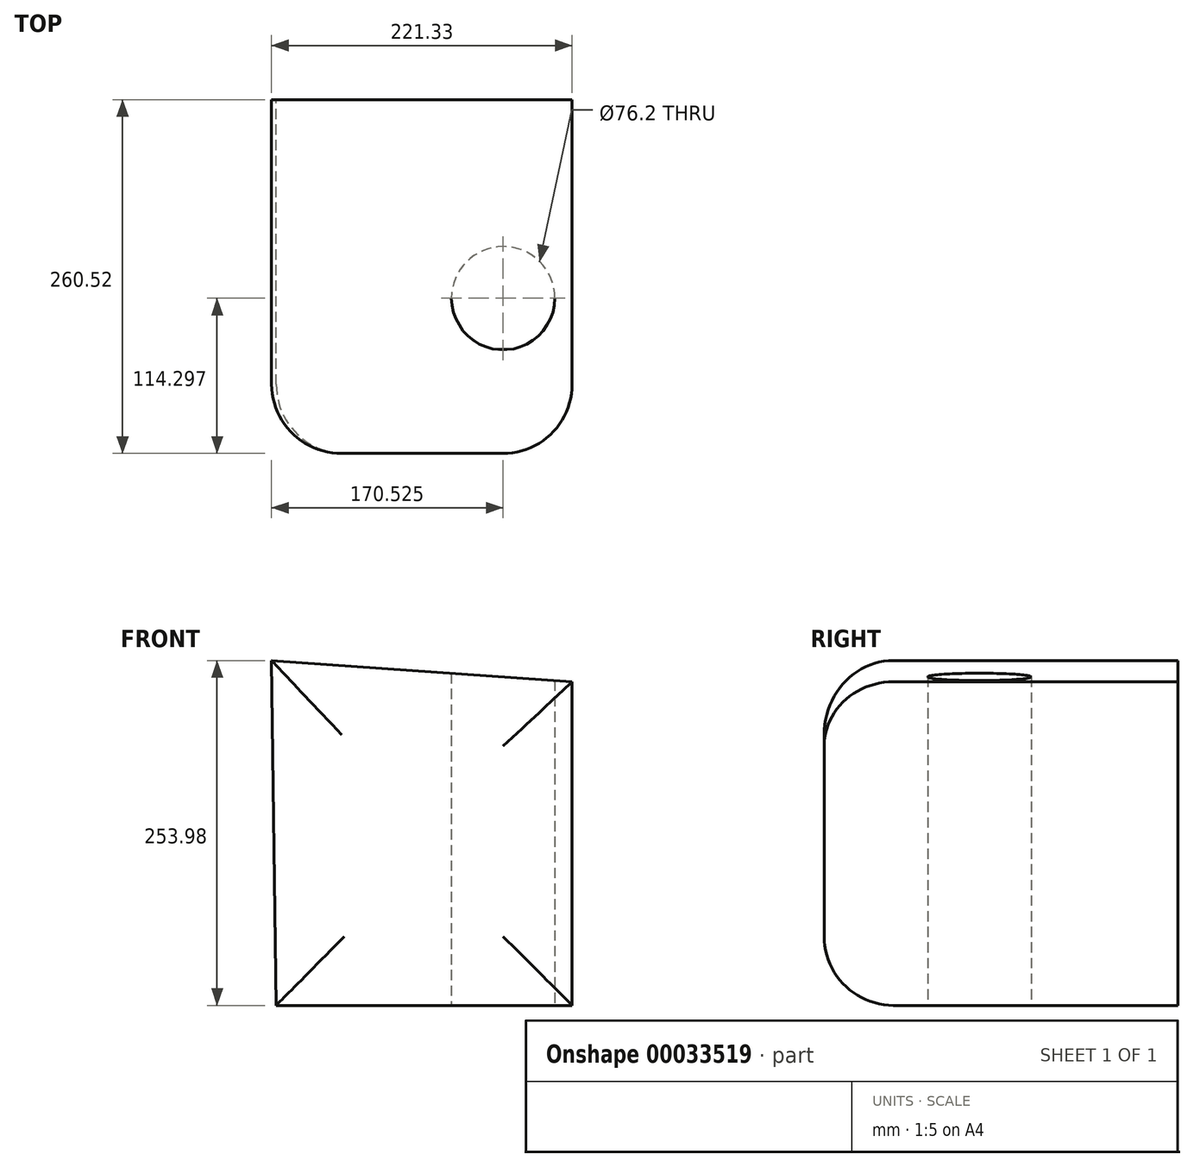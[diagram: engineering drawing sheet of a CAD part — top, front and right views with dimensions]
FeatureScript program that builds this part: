
annotation { "Feature Type Name" : "Feature", "Feature Type Description" : "" }
export const myFeature = defineFeature(function(context is Context, id is Id, definition is map)
    precondition{}
    {
        {
            var Q0;
            Q0=qCreatedBy(makeId("Front.planeOp"),FACE);
            var sketch = newSketch(context, id + "F2", { "sketchPlane" : qUnion([Q0])});
            skLineSegment(sketch, "E0", {"start": v(-110.2, -116.9) * mm, "end": v(107.67, -116.9) * mm});
            skLineSegment(sketch, "E1", {"start": v(107.67, -116.9) * mm, "end": v(107.67, 121.43) * mm});
            skLineSegment(sketch, "E2", {"start": v(107.67, 121.43) * mm, "end": v(-113.66, 137.07) * mm});
            skLineSegment(sketch, "E3", {"start": v(-113.66, 137.07) * mm, "end": v(-110.2, -116.9) * mm});
            skSolve(sketch);
        }
        {
            var Q0;
            Q0=makeQuery(id+"F2.imprint","IMPRINT",FACE,{"disambiguationData":[TD([[makeQuery(id+"F2.imprint","IMPRINT",EDGE,{"derivedFrom":sQuery(id+"F2.wireOp",EDGE,"E0")}),1.0]])]});
            extrude(context, id + "F3", {"entities" : qUnion([Q0]), "depth" : 260.52 * mm});
        }
        {
            var Q0;
            Q0=makeQuery(id+"F3.opExtrude","CAP_FACE",FACE,{"disambiguationData":[OSD([sQuery(id+"F2.wireOp",EDGE,"E0"),sQuery(id+"F2.wireOp",EDGE,"E1"),sQuery(id+"F2.wireOp",EDGE,"E2"),sQuery(id+"F2.wireOp",EDGE,"E3")])],"isStart":false});
            fillet(context, id + "F4", {"entities" : qUnion([Q0]), "radius" : 50.8 * mm, "tangentPropagation" : true, "allowEdgeOverflow" : false});
        }
        {
            var Q0;
            Q0=makeQuery(id+"F3.opExtrude","SWEPT_FACE",FACE,{"disambiguationData":[OSD([sQuery(id+"F2.wireOp",EDGE,"E0")])]});
            var sketch = newSketch(context, id + "F0", { "sketchPlane" : qUnion([Q0])});
            skCircle(sketch, "E4", {"center": v(56.87, 146.22) * mm, "radius": 38.1 * mm});
            skSolve(sketch);
        }
        {
            var Q0;
            Q0=makeQuery(id+"F0.imprint","IMPRINT",FACE,{"disambiguationData":[TD([[makeQuery(id+"F0.imprint","IMPRINT",EDGE,{"derivedFrom":sQuery(id+"F0.wireOp",EDGE,"E4")}),1.0]])]});
            extrude(context, id + "F1", {"entities" : qUnion([Q0]), "operationType" : NewBodyOperationType.REMOVE, "oppositeDirection" : true, "depth" : 285.44 * mm});
        }
    });
